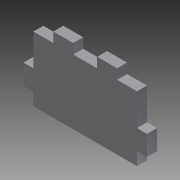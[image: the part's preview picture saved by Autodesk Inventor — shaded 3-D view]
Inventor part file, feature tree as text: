
AUTODESK INVENTOR PART (.ipt)
format: ipt  version: 2011 (Build 150239000, 239)  size: 92,160 bytes
history: native  units: in
note: dims shown in document units (in); Inventor stores cm internally (conversion verified against a paired STEP export)
features: extrude x1, sketch x1
ambient origin geometry x8: Origin, YZ Plane, XZ Plane, XY Plane, X Axis, Y Axis, Z Axis, Center Point
bodies: Solid1 (feature_tree)
feature tree (2):
  extrude  "Extrusion1"  Depth=2.6in
  sketch  "Sketch1"  dims[d0=1.625in d1=2.6in d2=0.5in d3=0.25in d4=0.5in d5=0.5in d6=0.5in d7=0.8in d8=0.25in d9=0.5in d10=0.8in d11=0.25in d12=0.25in d13=0.0in]
